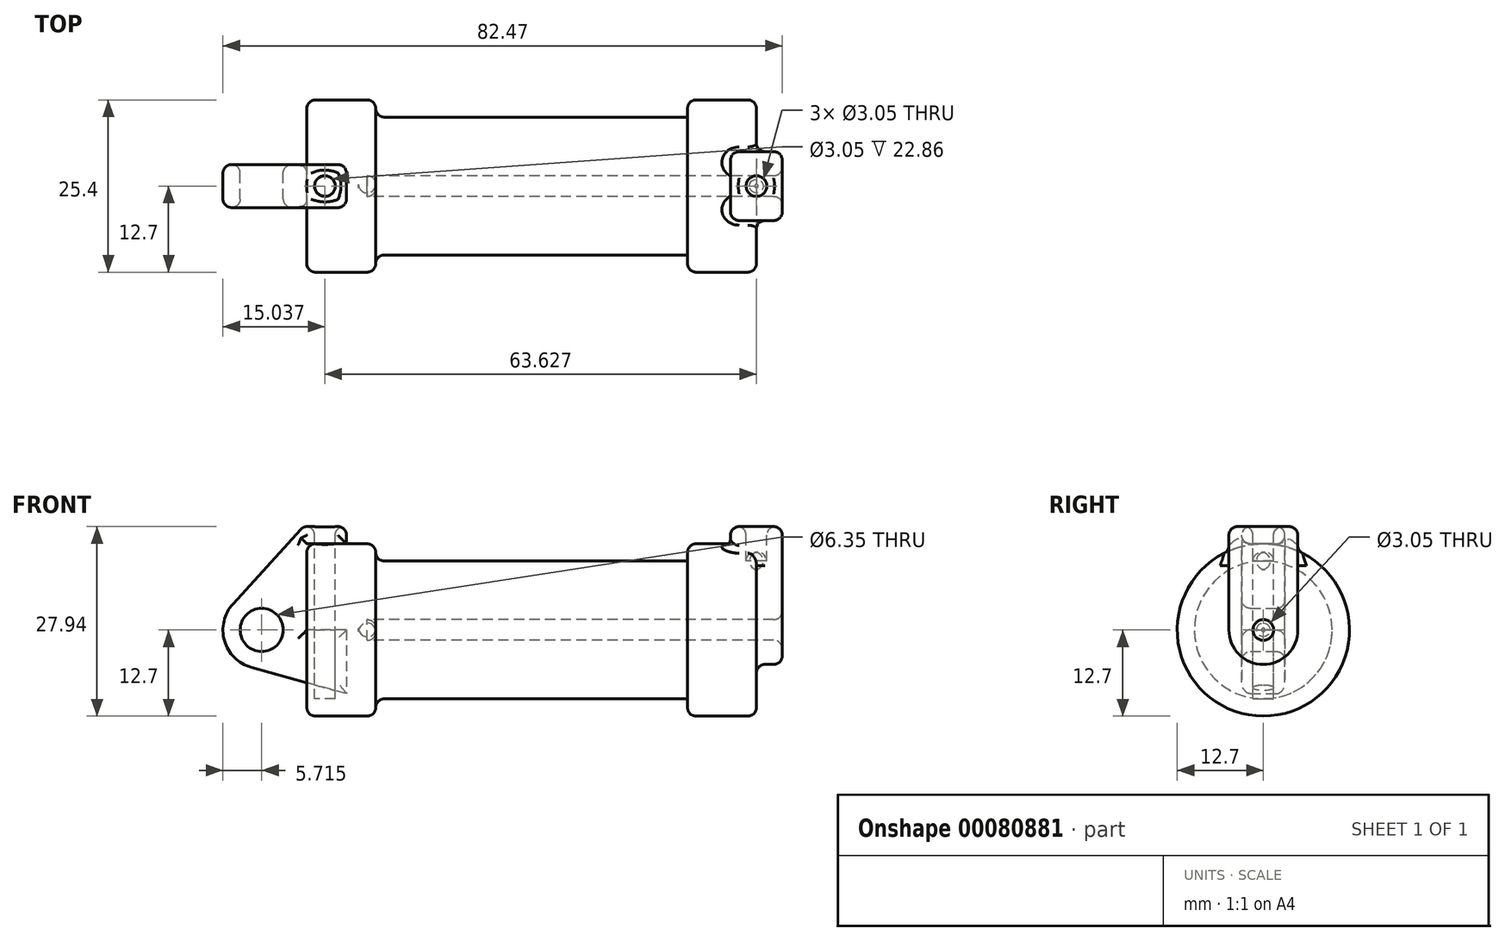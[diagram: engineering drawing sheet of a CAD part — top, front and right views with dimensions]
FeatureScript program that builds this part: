
annotation { "Feature Type Name" : "Feature", "Feature Type Description" : "" }
export const myFeature = defineFeature(function(context is Context, id is Id, definition is map)
    precondition{}
    {
        {
            var Q0;
            Q0=qCreatedBy(makeId("Front.planeOp"),FACE);
            var sketch = newSketch(context, id + "F0", { "sketchPlane" : qUnion([Q0])});
            skLineSegment(sketch, "E0", {"start": v(0, 0) * mm, "end": v(0, 12.7) * mm});
            skLineSegment(sketch, "E1", {"start": v(0, 12.7) * mm, "end": v(10.16, 12.7) * mm});
            skLineSegment(sketch, "E2", {"start": v(10.16, 12.7) * mm, "end": v(10.16, 10.16) * mm});
            skLineSegment(sketch, "E3", {"start": v(10.16, 10.16) * mm, "end": v(56.13, 10.16) * mm});
            skLineSegment(sketch, "E4", {"start": v(56.13, 10.16) * mm, "end": v(56.13, 12.7) * mm});
            skLineSegment(sketch, "E5", {"start": v(56.13, 12.7) * mm, "end": v(66.3, 12.7) * mm});
            skLineSegment(sketch, "E6", {"start": v(66.3, 12.7) * mm, "end": v(66.3, 0) * mm});
            skLineSegment(sketch, "E7", {"start": v(66.3, 0) * mm, "end": v(0, 0) * mm});
            skLineSegment(sketch, "E8", {"start": v(5.84, 15.24) * mm, "end": v(-0.5, 15.24) * mm});
            skLineSegment(sketch, "E9", {"start": v(-0.5, 15.24) * mm, "end": v(-10.88, 3.85) * mm});
            skLineSegment(sketch, "E10", {"start": v(0, 0) * mm, "end": v(-6.65, 0) * mm});
            skCircle(sketch, "E11", {"center": v(-6.65, 0) * mm, "radius": 5.72 * mm});
            skCircle(sketch, "E12", {"center": v(-6.65, 0) * mm, "radius": 3.18 * mm});
            skLineSegment(sketch, "E13", {"start": v(5.84, 15.24) * mm, "end": v(5.84, -9.4) * mm});
            skLineSegment(sketch, "E14", {"start": v(5.84, -9.4) * mm, "end": v(-8.18, -5.5) * mm});
            skSolve(sketch);
        }
        {
            var Q0;
            {var subQ0=sQuery(id+"F0.wireOp",EDGE,"E2");Q0=makeQuery(id+"F0.imprint","IMPRINT",FACE,{"disambiguationData":[TD([[makeQuery(id+"F0.imprint","IMPRINT",EDGE,{"derivedFrom":subQ0}),-1.0]])]});}
            var Q1;
            {var subQ0=sQuery(id+"F0.wireOp",EDGE,"E0");Q1=makeQuery(id+"F0.imprint","IMPRINT",FACE,{"disambiguationData":[TD([[makeQuery(id+"F0.imprint","IMPRINT",EDGE,{"derivedFrom":subQ0}),-1.0]])]});}
            var Q2;
            Q2=sQuery(id+"F0.wireOp",EDGE,"E7");
            revolve(context, id + "F1", {"entities" : qUnion([Q0, Q1]), "axis" : qUnion([Q2]), "revolveType" : RevolveType.FULL});
        }
        {
            var Q0;
            {var subQ3=sQuery(id+"F0.wireOp",EDGE,"E0");Q0=makeQuery(id+"F0.imprint","IMPRINT",FACE,{"disambiguationData":[TD([[makeQuery(id+"F0.imprint","IMPRINT",EDGE,{"derivedFrom":subQ3}),1.0]])]});}
            var Q1;
            {var subQ4=sQuery(id+"F0.wireOp",EDGE,"E12");Q1=makeQuery(id+"F0.imprint","IMPRINT",FACE,{"disambiguationData":[TD([[makeQuery(id+"F0.imprint","IMPRINT",EDGE,{"derivedFrom":subQ4}),-1.0]])]});}
            var Q2;
            {var subQ0=sQuery(id+"F0.wireOp",EDGE,"E14");Q2=makeQuery(id+"F0.imprint","IMPRINT",FACE,{"disambiguationData":[TD([[makeQuery(id+"F0.imprint","IMPRINT",EDGE,{"derivedFrom":subQ0}),-1.0]])]});}
            extrude(context, id + "F2", {"entities" : qUnion([Q0, Q1, Q2]), "endBound" : BoundingType.SYMMETRIC, "depth" : 6.35 * mm});
        }
        {
            var Q0;
            Q0=makeQuery(id+"F1.opRevolve","SWEPT_FACE",FACE,{"disambiguationData":[OSD([sQuery(id+"F0.wireOp",EDGE,"E6")])]});
            var sketch = newSketch(context, id + "F3", { "sketchPlane" : qUnion([Q0])});
            skCircle(sketch, "E15", {"center": v(0, 0) * mm, "radius": 1.52 * mm});
            skCircle(sketch, "E16", {"center": v(0, 0) * mm, "radius": 5.08 * mm});
            skLineSegment(sketch, "E17", {"start": v(5.08, 0) * mm, "end": v(5.08, 15.24) * mm});
            skLineSegment(sketch, "E18", {"start": v(-5.08, 0) * mm, "end": v(-5.08, 15.24) * mm});
            skLineSegment(sketch, "E19", {"start": v(-5.08, 15.24) * mm, "end": v(5.08, 15.24) * mm});
            skSolve(sketch);
        }
        {
            var Q0;
            Q0 = qSketchRegion(id + "F3", true);
            extrude(context, id + "F4", {"entities" : qUnion([Q0]), "operationType" : NewBodyOperationType.ADD, "endBound" : BoundingType.SYMMETRIC, "depth" : 7.62 * mm});
        }
        {
            var Q0;
            Q0=makeQuery(id+"F2.opExtrude","SWEPT_FACE",FACE,{"disambiguationData":[OSD([sQuery(id+"F0.wireOp",EDGE,"E8")])]});
            var sketch = newSketch(context, id + "F5", { "sketchPlane" : qUnion([Q0])});
            skLineSegment(sketch, "E20", {"start": v(-0.5, 0) * mm, "end": v(5.84, 0) * mm});
            skCircle(sketch, "E21", {"center": v(2.67, 0) * mm, "radius": 1.52 * mm});
            skSolve(sketch);
        }
        {
            var Q0;
            {var subQ0=sQuery(id+"F5.wireOp",EDGE,"E21");var subQ1=sQuery(id+"F5.wireOp",EDGE,"E20");var subQ2=makeQuery(id+"F5.imprint","INTERSECT",VERTEX,{"disambiguationData":[OD(0.0)],"derivedFrom":[subQ1,subQ0]});Q0=makeQuery(id+"F5.imprint","IMPRINT",FACE,{"disambiguationData":[TD([[makeQuery(id+"F5.imprint","IMPRINT",EDGE,{"disambiguationData":[TD([[subQ2,-1.0]])],"derivedFrom":subQ1}),1.0]])]});}
            var Q1;
            {var subQ0=sQuery(id+"F5.wireOp",EDGE,"E21");var subQ1=sQuery(id+"F5.wireOp",EDGE,"E20");var subQ2=makeQuery(id+"F5.imprint","INTERSECT",VERTEX,{"disambiguationData":[OD(0.0)],"derivedFrom":[subQ1,subQ0]});Q1=makeQuery(id+"F5.imprint","IMPRINT",FACE,{"disambiguationData":[TD([[makeQuery(id+"F5.imprint","IMPRINT",EDGE,{"disambiguationData":[TD([[subQ2,-1.0]])],"derivedFrom":subQ1}),-1.0]])]});}
            extrude(context, id + "F6", {"entities" : qUnion([Q0, Q1]), "operationType" : NewBodyOperationType.REMOVE, "oppositeDirection" : true, "depth" : 25.4 * mm});
        }
        {
            var Q0;
            Q0=makeQuery(id+"F4.opExtrude","SWEPT_FACE",FACE,{"disambiguationData":[OSD([sQuery(id+"F3.wireOp",EDGE,"E19")])]});
            var sketch = newSketch(context, id + "F7", { "sketchPlane" : qUnion([Q0])});
            skLineSegment(sketch, "E22", {"start": v(62.48, 0) * mm, "end": v(70.1, 0) * mm});
            skCircle(sketch, "E23", {"center": v(66.3, 0) * mm, "radius": 1.52 * mm});
            skSolve(sketch);
        }
        {
            var Q0;
            {var subQ0=sQuery(id+"F7.wireOp",EDGE,"E23");var subQ1=sQuery(id+"F7.wireOp",EDGE,"E22");var subQ2=makeQuery(id+"F7.imprint","INTERSECT",VERTEX,{"disambiguationData":[OD(0.0)],"derivedFrom":[subQ1,subQ0]});Q0=makeQuery(id+"F7.imprint","IMPRINT",FACE,{"disambiguationData":[TD([[makeQuery(id+"F7.imprint","IMPRINT",EDGE,{"disambiguationData":[TD([[subQ2,-1.0]])],"derivedFrom":subQ1}),1.0]])]});}
            var Q1;
            {var subQ0=sQuery(id+"F7.wireOp",EDGE,"E23");var subQ1=sQuery(id+"F7.wireOp",EDGE,"E22");var subQ2=makeQuery(id+"F7.imprint","INTERSECT",VERTEX,{"disambiguationData":[OD(0.0)],"derivedFrom":[subQ1,subQ0]});Q1=makeQuery(id+"F7.imprint","IMPRINT",FACE,{"disambiguationData":[TD([[makeQuery(id+"F7.imprint","IMPRINT",EDGE,{"disambiguationData":[TD([[subQ2,-1.0]])],"derivedFrom":subQ1}),-1.0]])]});}
            extrude(context, id + "F8", {"entities" : qUnion([Q0, Q1]), "operationType" : NewBodyOperationType.REMOVE, "oppositeDirection" : true, "depth" : 6.35 * mm});
        }
        {
            var Q0;
            Q0=makeQuery(id+"F4.opExtrude","CAP_FACE",FACE,{"disambiguationData":[OSD([sQuery(id+"F3.wireOp",EDGE,"E15"),sQuery(id+"F3.wireOp",EDGE,"E16"),sQuery(id+"F3.wireOp",EDGE,"E17"),sQuery(id+"F3.wireOp",EDGE,"E18"),sQuery(id+"F3.wireOp",EDGE,"E19")])],"isStart":false});
            var sketch = newSketch(context, id + "F9", { "sketchPlane" : qUnion([Q0])});
            skCircle(sketch, "E24", {"center": v(0, 0) * mm, "radius": 1.52 * mm});
            skSolve(sketch);
        }
        {
            var Q0;
            Q0 = qSketchRegion(id + "F9", true);
            extrude(context, id + "F10", {"entities" : qUnion([Q0]), "operationType" : NewBodyOperationType.REMOVE, "oppositeDirection" : true, "depth" : 62.46 * mm});
        }
        {
            var Q0;
            Q0=makeQuery(id+"F1.opRevolve","SWEPT_EDGE",EDGE,{"disambiguationData":[OSD([sQuery(id+"F0.wireOp",EDGE,"E1"),sQuery(id+"F0.wireOp",EDGE,"E2")])]});
            var Q1;
            Q1=makeQuery(id+"F1.opRevolve","SWEPT_EDGE",EDGE,{"disambiguationData":[OSD([sQuery(id+"F0.wireOp",EDGE,"E4"),sQuery(id+"F0.wireOp",EDGE,"E5")])]});
            var Q2;
            Q2=makeQuery(id+"F1.opRevolve","SWEPT_EDGE",EDGE,{"disambiguationData":[OSD([sQuery(id+"F0.wireOp",EDGE,"E2"),sQuery(id+"F0.wireOp",EDGE,"E3")])]});
            var Q3;
            Q3=makeQuery(id+"F1.opRevolve","SWEPT_EDGE",EDGE,{"disambiguationData":[OSD([sQuery(id+"F0.wireOp",EDGE,"E0"),sQuery(id+"F0.wireOp",EDGE,"E1")])]});
            var Q4;
            Q4=makeQuery(id+"F1.opRevolve","SWEPT_EDGE",EDGE,{"disambiguationData":[OSD([sQuery(id+"F0.wireOp",EDGE,"E5"),sQuery(id+"F0.wireOp",EDGE,"E6")])]});
            fillet(context, id + "F11", {"entities" : qUnion([Q0, Q1, Q2, Q3, Q4]), "radius" : 1.27 * mm, "tangentPropagation" : true, "allowEdgeOverflow" : false});
        }
        {
            var Q0;
            Q0=makeQuery(id+"F2.opExtrude","SWEPT_FACE",FACE,{"disambiguationData":[OSD([sQuery(id+"F0.wireOp",EDGE,"E8")])]});
            var Q1;
            Q1=makeQuery(id+"F2.opExtrude","SWEPT_FACE",FACE,{"disambiguationData":[OSD([sQuery(id+"F0.wireOp",EDGE,"E9")])]});
            var Q2;
            Q2=makeQuery(id+"F2.opExtrude","CAP_FACE",FACE,{"disambiguationData":[OSD([sQuery(id+"F0.wireOp",EDGE,"E0"),sQuery(id+"F0.wireOp",EDGE,"E1"),sQuery(id+"F0.wireOp",EDGE,"E7"),sQuery(id+"F0.wireOp",EDGE,"E8"),sQuery(id+"F0.wireOp",EDGE,"E9"),sQuery(id+"F0.wireOp",EDGE,"E11"),sQuery(id+"F0.wireOp",EDGE,"E12"),sQuery(id+"F0.wireOp",EDGE,"E13"),sQuery(id+"F0.wireOp",EDGE,"E14")])],"isStart":true});
            var Q3;
            Q3=makeQuery(id+"F11.opFillet","BLEND_FACE",FACE,{"disambiguationData":[OSD([sQuery(id+"F0.wireOp",EDGE,"E0"),sQuery(id+"F0.wireOp",EDGE,"E1")])]});
            var Q4;
            Q4=makeQuery(id+"F2.opExtrude","CAP_FACE",FACE,{"disambiguationData":[OSD([sQuery(id+"F0.wireOp",EDGE,"E0"),sQuery(id+"F0.wireOp",EDGE,"E1"),sQuery(id+"F0.wireOp",EDGE,"E7"),sQuery(id+"F0.wireOp",EDGE,"E8"),sQuery(id+"F0.wireOp",EDGE,"E9"),sQuery(id+"F0.wireOp",EDGE,"E11"),sQuery(id+"F0.wireOp",EDGE,"E12"),sQuery(id+"F0.wireOp",EDGE,"E13"),sQuery(id+"F0.wireOp",EDGE,"E14")])],"isStart":false});
            fillet(context, id + "F12", {"entities" : qUnion([Q0, Q1, Q2, Q3, Q4]), "radius" : 1.27 * mm, "tangentPropagation" : true, "allowEdgeOverflow" : false});
        }
        {
            var Q0;
            Q0=makeQuery(id+"F4.opExtrude","SWEPT_FACE",FACE,{"disambiguationData":[OSD([sQuery(id+"F3.wireOp",EDGE,"E19")])]});
            var Q1;
            Q1=makeQuery(id+"F8.boolean.opBoolean","COPY",FACE,{"derivedFrom":makeQuery(id+"F8.opExtrude","SWEPT_FACE",FACE,{"disambiguationData":[OSD([sQuery(id+"F7.wireOp",EDGE,"E23")])]})});
            var Q2;
            Q2=makeQuery(id+"F4.boolean.opBoolean","SPLIT",FACE,{"disambiguationData":[TD([makeQuery(id+"F1.opRevolve","SWEPT_FACE",FACE,{"disambiguationData":[OSD([sQuery(id+"F0.wireOp",EDGE,"E5")])]})])],"derivedFrom":makeQuery(id+"F1.opRevolve","SWEPT_FACE",FACE,{"disambiguationData":[OSD([sQuery(id+"F0.wireOp",EDGE,"E6")])]})});
            var Q3;
            Q3=makeQuery(id+"F10.boolean.opBoolean","MERGE",FACE,{"derivedFrom":[makeQuery(id+"F4.opExtrude","SWEPT_FACE",FACE,{"disambiguationData":[OSD([sQuery(id+"F3.wireOp",EDGE,"E15")])]}),makeQuery(id+"F10.opExtrude","SWEPT_FACE",FACE,{"disambiguationData":[OSD([sQuery(id+"F9.wireOp",EDGE,"E24")])]})]});
            var Q4;
            Q4=makeQuery(id+"F4.opExtrude","CAP_EDGE",EDGE,{"disambiguationData":[OSD([sQuery(id+"F3.wireOp",EDGE,"E15")])],"isStart":false});
            var Q5;
            Q5=makeQuery(id+"F4.opExtrude","SWEPT_FACE",FACE,{"disambiguationData":[OSD([sQuery(id+"F3.wireOp",EDGE,"E18")])]});
            var Q6;
            Q6=makeQuery(id+"F4.opExtrude","SWEPT_FACE",FACE,{"disambiguationData":[OSD([sQuery(id+"F3.wireOp",EDGE,"E17")])]});
            var Q7;
            Q7=makeQuery(id+"F4.opExtrude","SWEPT_FACE",FACE,{"disambiguationData":[OSD([sQuery(id+"F3.wireOp",EDGE,"E16")])]});
            fillet(context, id + "F13", {"entities" : qUnion([Q0, Q1, Q2, Q3, Q4, Q5, Q6, Q7]), "radius" : 1.27 * mm, "tangentPropagation" : true, "allowEdgeOverflow" : false});
        }
    });
